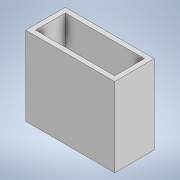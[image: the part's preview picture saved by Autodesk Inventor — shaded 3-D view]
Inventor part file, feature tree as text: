
AUTODESK INVENTOR PART (.ipt)
format: ipt  version: 2022.1 (Build 261234000, 234)  size: 96,768 bytes
history: native  units: in
note: dims shown in document units (in); Inventor stores cm internally (conversion verified against a paired STEP export)
features: extrude x1, sketch x1
ambient origin geometry x8: Origin, YZ Plane, XZ Plane, XY Plane, X Axis, Y Axis, Z Axis, Center Point
bodies: Solid1 (feature_tree)
feature tree (2):
  extrude  "Extrusion1"  Depth=2.25in
  sketch  "Sketch1"  dims[d0=1.0in d1=2.25in d2=0.125in d3=0.125in d4=2.0in d5=0.0in]
